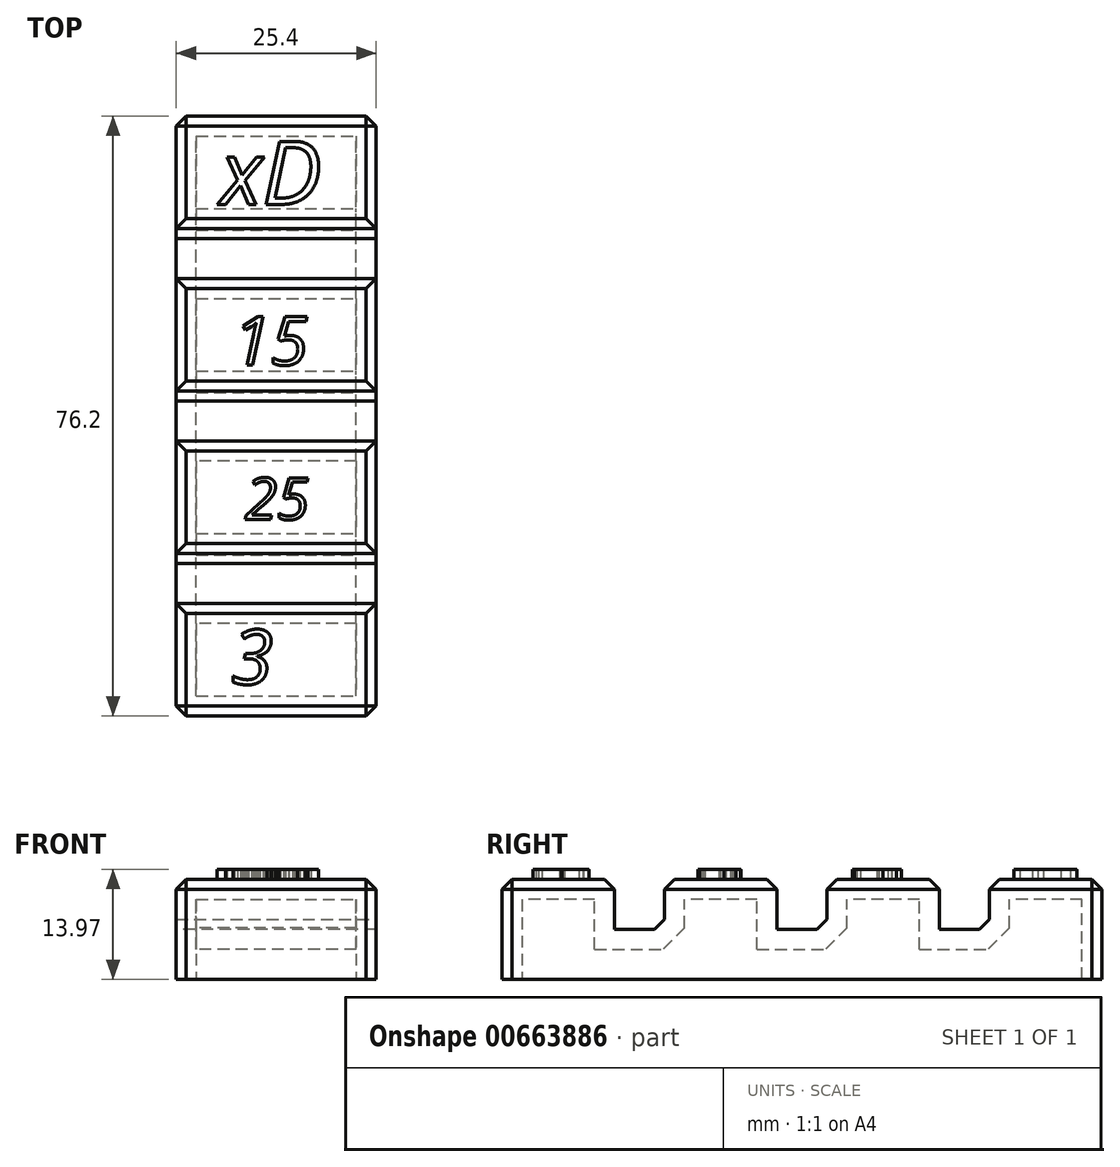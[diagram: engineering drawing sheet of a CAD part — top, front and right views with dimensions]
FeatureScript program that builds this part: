
annotation { "Feature Type Name" : "Feature", "Feature Type Description" : "" }
export const myFeature = defineFeature(function(context is Context, id is Id, definition is map)
    precondition{}
    {
        {
            var Q0;
            Q0=qCreatedBy(makeId("Top.planeOp"),FACE);
            var sketch = newSketch(context, id + "F0", { "sketchPlane" : qUnion([Q0])});
            skLineSegment(sketch, "E0.bottom", {"start": v(-12.7, -38.1) * mm, "end": v(12.7, -38.1) * mm});
            skLineSegment(sketch, "E0.top", {"start": v(-12.7, 38.1) * mm, "end": v(12.7, 38.1) * mm});
            skLineSegment(sketch, "E0.left", {"start": v(-12.7, -38.1) * mm, "end": v(-12.7, 38.1) * mm});
            skLineSegment(sketch, "E0.right", {"start": v(12.7, -38.1) * mm, "end": v(12.7, 38.1) * mm});
            skPoint(sketch, "E0.middle", {"position": v(0, 0) * mm});
            skSolve(sketch);
        }
        {
            var Q0;
            Q0 = qSketchRegion(id + "F0", true);
            extrude(context, id + "F1", {"entities" : qUnion([Q0]), "depth" : 12.7 * mm, "offsetDistance" : 25.4 * mm});
        }
        {
            var Q0;
            Q0=makeQuery(id+"F1.opExtrude","SWEPT_FACE",FACE,{"disambiguationData":[OSD([sQuery(id+"F0.wireOp",EDGE,"E0.left")])]});
            var sketch = newSketch(context, id + "F2", { "sketchPlane" : qUnion([Q0])});
            skLineSegment(sketch, "E1", {"start": v(-38.1, 6.35) * mm, "end": v(38.1, 6.35) * mm, "construction": true});
            skPoint(sketch, "E1.startSnap0", {"position": v(-38.1, 6.35) * mm});
            skLineSegment(sketch, "E2.bottom", {"start": v(3.18, 6.35) * mm, "end": v(-3.18, 6.35) * mm});
            skLineSegment(sketch, "E2.top", {"start": v(3.18, 19.05) * mm, "end": v(-3.18, 19.05) * mm});
            skLineSegment(sketch, "E2.left", {"start": v(3.18, 6.35) * mm, "end": v(3.18, 19.05) * mm});
            skLineSegment(sketch, "E2.right", {"start": v(-3.18, 6.35) * mm, "end": v(-3.18, 19.05) * mm});
            skPoint(sketch, "E2.middle", {"position": v(0, 12.7) * mm});
            skLineSegment(sketch, "E3.bottom", {"start": v(23.81, 6.35) * mm, "end": v(17.46, 6.35) * mm});
            skLineSegment(sketch, "E3.top", {"start": v(23.81, 19.05) * mm, "end": v(17.46, 19.05) * mm});
            skLineSegment(sketch, "E3.left", {"start": v(23.81, 6.35) * mm, "end": v(23.81, 19.05) * mm});
            skLineSegment(sketch, "E3.right", {"start": v(17.46, 6.35) * mm, "end": v(17.46, 19.05) * mm});
            skPoint(sketch, "E3.middle", {"position": v(20.64, 12.7) * mm});
            skLineSegment(sketch, "E4.bottom", {"start": v(-17.46, 6.35) * mm, "end": v(-23.81, 6.35) * mm});
            skLineSegment(sketch, "E4.top", {"start": v(-17.46, 19.05) * mm, "end": v(-23.81, 19.05) * mm});
            skLineSegment(sketch, "E4.left", {"start": v(-17.46, 6.35) * mm, "end": v(-17.46, 19.05) * mm});
            skLineSegment(sketch, "E4.right", {"start": v(-23.81, 6.35) * mm, "end": v(-23.81, 19.05) * mm});
            skPoint(sketch, "E4.middle", {"position": v(-20.64, 12.7) * mm});
            skSolve(sketch);
        }
        {
            var Q0;
            Q0 = qSketchRegion(id + "F2", true);
            extrude(context, id + "F3", {"entities" : qUnion([Q0]), "operationType" : NewBodyOperationType.REMOVE, "endBound" : BoundingType.THROUGH_ALL, "oppositeDirection" : true, "depth" : 25.4 * mm, "offsetDistance" : 25.4 * mm});
        }
        {
            var Q0;
            {var subQ0=sQuery(id+"F0.wireOp",EDGE,"E0.top");var subQ1=sQuery(id+"F0.wireOp",EDGE,"E0.left");var subQ2=sQuery(id+"F0.wireOp",EDGE,"E0.right");Q0=makeQuery(id+"F3.boolean.opBoolean","SPLIT",FACE,{"disambiguationData":[TD([makeQuery(id+"F1.opExtrude","SWEPT_FACE",FACE,{"disambiguationData":[OSD([subQ0])]})])],"derivedFrom":makeQuery(id+"F1.opExtrude","CAP_FACE",FACE,{"disambiguationData":[OSD([sQuery(id+"F0.wireOp",EDGE,"E0.bottom"),subQ0,subQ1,subQ2])],"isStart":false})});}
            var Q1;
            {var subQ0=sQuery(id+"F0.wireOp",EDGE,"E0.left");var subQ1=sQuery(id+"F0.wireOp",EDGE,"E0.right");Q1=makeQuery(id+"F3.boolean.opBoolean","SPLIT",FACE,{"disambiguationData":[TD([makeQuery(id+"F3.opExtrude","SWEPT_FACE",FACE,{"disambiguationData":[OSD([sQuery(id+"F2.wireOp",EDGE,"E2.right")])]})])],"derivedFrom":makeQuery(id+"F1.opExtrude","CAP_FACE",FACE,{"disambiguationData":[OSD([sQuery(id+"F0.wireOp",EDGE,"E0.bottom"),sQuery(id+"F0.wireOp",EDGE,"E0.top"),subQ0,subQ1])],"isStart":false})});}
            var Q2;
            {var subQ0=sQuery(id+"F0.wireOp",EDGE,"E0.left");var subQ1=sQuery(id+"F0.wireOp",EDGE,"E0.right");Q2=makeQuery(id+"F3.boolean.opBoolean","SPLIT",FACE,{"disambiguationData":[TD([makeQuery(id+"F3.opExtrude","SWEPT_FACE",FACE,{"disambiguationData":[OSD([sQuery(id+"F2.wireOp",EDGE,"E2.left")])]})])],"derivedFrom":makeQuery(id+"F1.opExtrude","CAP_FACE",FACE,{"disambiguationData":[OSD([sQuery(id+"F0.wireOp",EDGE,"E0.bottom"),sQuery(id+"F0.wireOp",EDGE,"E0.top"),subQ0,subQ1])],"isStart":false})});}
            var Q3;
            Q3=makeQuery(id+"F1.opExtrude","CAP_EDGE",EDGE,{"disambiguationData":[OSD([sQuery(id+"F0.wireOp",EDGE,"E0.bottom")])],"isStart":false});
            var Q4;
            {var subQ0=sQuery(id+"F0.wireOp",EDGE,"E0.bottom");var subQ1=sQuery(id+"F0.wireOp",EDGE,"E0.right");var subQ2=sQuery(id+"F0.wireOp",EDGE,"E0.left");Q4=makeQuery(id+"F3.boolean.opBoolean","SPLIT",FACE,{"disambiguationData":[TD([makeQuery(id+"F1.opExtrude","SWEPT_FACE",FACE,{"disambiguationData":[OSD([subQ0])]})])],"derivedFrom":makeQuery(id+"F1.opExtrude","CAP_FACE",FACE,{"disambiguationData":[OSD([subQ0,sQuery(id+"F0.wireOp",EDGE,"E0.top"),subQ2,subQ1])],"isStart":false})});}
            var Q5;
            Q5=makeQuery(id+"F3.boolean.opBoolean","COPY",EDGE,{"derivedFrom":makeQuery(id+"F3.opExtrude","SWEPT_EDGE",EDGE,{"disambiguationData":[OSD([sQuery(id+"F2.wireOp",EDGE,"E4.bottom"),sQuery(id+"F2.wireOp",EDGE,"E4.right")])]})});
            var Q6;
            Q6=makeQuery(id+"F3.boolean.opBoolean","COPY",EDGE,{"derivedFrom":makeQuery(id+"F3.opExtrude","CAP_EDGE",EDGE,{"disambiguationData":[OSD([sQuery(id+"F2.wireOp",EDGE,"E2.bottom")])],"isStart":true})});
            var Q7;
            Q7=makeQuery(id+"F3.boolean.opBoolean","COPY",EDGE,{"derivedFrom":makeQuery(id+"F3.opExtrude","CAP_EDGE",EDGE,{"disambiguationData":[OSD([sQuery(id+"F2.wireOp",EDGE,"E3.bottom")])],"isStart":true})});
            var Q8;
            Q8=makeQuery(id+"F3.boolean.opBoolean","COPY",EDGE,{"derivedFrom":makeQuery(id+"F3.opExtrude","CAP_EDGE",EDGE,{"disambiguationData":[OSD([sQuery(id+"F2.wireOp",EDGE,"E4.bottom")])],"isStart":true})});
            var Q9;
            Q9=makeQuery(id+"F3.boolean.opBoolean","COPY",EDGE,{"derivedFrom":makeQuery(id+"F3.opExtrude","SWEPT_EDGE",EDGE,{"disambiguationData":[OSD([sQuery(id+"F2.wireOp",EDGE,"E2.bottom"),sQuery(id+"F2.wireOp",EDGE,"E2.right")])]})});
            var Q10;
            Q10=makeQuery(id+"F3.boolean.opBoolean","COPY",EDGE,{"derivedFrom":makeQuery(id+"F3.opExtrude","SWEPT_EDGE",EDGE,{"disambiguationData":[OSD([sQuery(id+"F2.wireOp",EDGE,"E3.bottom"),sQuery(id+"F2.wireOp",EDGE,"E3.right")])]})});
            var Q11;
            Q11=makeQuery(id+"F1.opExtrude","SWEPT_EDGE",EDGE,{"disambiguationData":[OSD([sQuery(id+"F0.wireOp",EDGE,"E0.top"),sQuery(id+"F0.wireOp",EDGE,"E0.left")])]});
            var Q12;
            Q12=makeQuery(id+"F1.opExtrude","SWEPT_EDGE",EDGE,{"disambiguationData":[OSD([sQuery(id+"F0.wireOp",EDGE,"E0.bottom"),sQuery(id+"F0.wireOp",EDGE,"E0.left")])]});
            var Q13;
            Q13=makeQuery(id+"F1.opExtrude","SWEPT_EDGE",EDGE,{"disambiguationData":[OSD([sQuery(id+"F0.wireOp",EDGE,"E0.bottom"),sQuery(id+"F0.wireOp",EDGE,"E0.right")])]});
            var Q14;
            Q14=makeQuery(id+"F1.opExtrude","SWEPT_EDGE",EDGE,{"disambiguationData":[OSD([sQuery(id+"F0.wireOp",EDGE,"E0.top"),sQuery(id+"F0.wireOp",EDGE,"E0.right")])]});
            chamfer(context, id + "F4", {"entities" : qUnion([Q0, Q1, Q2, Q3, Q4, Q5, Q6, Q7, Q8, Q9, Q10, Q11, Q12, Q13, Q14]), "width" : 1.27 * mm, "tangentPropagation" : true});
        }
        {
            var Q0;
            Q0=makeQuery(id+"F1.opExtrude","CAP_FACE",FACE,{"disambiguationData":[OSD([sQuery(id+"F0.wireOp",EDGE,"E0.bottom"),sQuery(id+"F0.wireOp",EDGE,"E0.top"),sQuery(id+"F0.wireOp",EDGE,"E0.left"),sQuery(id+"F0.wireOp",EDGE,"E0.right")])],"isStart":true});
            shell(context, id + "F5", {"entities" : qUnion([Q0]), "thickness" : 2.54 * mm});
        }
        {
            var Q0;
            {var subQ0=sQuery(id+"F0.wireOp",EDGE,"E0.top");var subQ1=sQuery(id+"F0.wireOp",EDGE,"E0.left");var subQ2=sQuery(id+"F0.wireOp",EDGE,"E0.right");Q0=makeQuery(id+"F3.boolean.opBoolean","SPLIT",FACE,{"disambiguationData":[TD([makeQuery(id+"F1.opExtrude","SWEPT_FACE",FACE,{"disambiguationData":[OSD([subQ0])]})])],"derivedFrom":makeQuery(id+"F1.opExtrude","CAP_FACE",FACE,{"disambiguationData":[OSD([sQuery(id+"F0.wireOp",EDGE,"E0.bottom"),subQ0,subQ1,subQ2])],"isStart":false})});}
            var sketch = newSketch(context, id + "F6", { "sketchPlane" : qUnion([Q0])});
            skText(sketch, "E5", { "text": "3", "fontName": "OpenSans-Italic.ttf"});
            skLineSegment(sketch, "E6", {"start": v(0, -30.59) * mm, "end": v(11.37, -30.59) * mm, "construction": true});
            skLineSegment(sketch, "E7", {"start": v(0, -30.59) * mm, "end": v(-11.38, -30.59) * mm, "construction": true});
            const initialGuessF6  = {"E5": [-0.0057, -0.03407, 1, 0, 0.00696]};
            skSetInitialGuess(sketch, initialGuessF6);
            skSolve(sketch);
        }
        {
            var Q0;
            Q0 = qSketchRegion(id + "F6", true);
            extrude(context, id + "F7", {"entities" : qUnion([Q0]), "operationType" : NewBodyOperationType.ADD, "depth" : 1.27 * mm, "offsetDistance" : 25.4 * mm});
        }
        {
            var Q0;
            {var subQ0=sQuery(id+"F0.wireOp",EDGE,"E0.left");var subQ1=sQuery(id+"F0.wireOp",EDGE,"E0.right");Q0=makeQuery(id+"F3.boolean.opBoolean","SPLIT",FACE,{"disambiguationData":[TD([makeQuery(id+"F3.opExtrude","SWEPT_FACE",FACE,{"disambiguationData":[OSD([sQuery(id+"F2.wireOp",EDGE,"E2.left")])]})])],"derivedFrom":makeQuery(id+"F1.opExtrude","CAP_FACE",FACE,{"disambiguationData":[OSD([sQuery(id+"F0.wireOp",EDGE,"E0.bottom"),sQuery(id+"F0.wireOp",EDGE,"E0.top"),subQ0,subQ1])],"isStart":false})});}
            var sketch = newSketch(context, id + "F8", { "sketchPlane" : qUnion([Q0])});
            skText(sketch, "E8", { "text": "25", "fontName": "OpenSans-Italic.ttf"});
            const initialGuessF8  = {"E8": [-0.004, -0.01316, 1, 0, 0.00535]};
            skSetInitialGuess(sketch, initialGuessF8);
            skSolve(sketch);
        }
        {
            var Q0;
            Q0 = qSketchRegion(id + "F8", true);
            extrude(context, id + "F9", {"entities" : qUnion([Q0]), "operationType" : NewBodyOperationType.ADD, "depth" : 1.27 * mm, "offsetDistance" : 25.4 * mm});
        }
        {
            var Q0;
            {var subQ0=sQuery(id+"F0.wireOp",EDGE,"E0.left");var subQ1=sQuery(id+"F0.wireOp",EDGE,"E0.right");Q0=makeQuery(id+"F3.boolean.opBoolean","SPLIT",FACE,{"disambiguationData":[TD([makeQuery(id+"F3.opExtrude","SWEPT_FACE",FACE,{"disambiguationData":[OSD([sQuery(id+"F2.wireOp",EDGE,"E2.right")])]})])],"derivedFrom":makeQuery(id+"F1.opExtrude","CAP_FACE",FACE,{"disambiguationData":[OSD([sQuery(id+"F0.wireOp",EDGE,"E0.bottom"),sQuery(id+"F0.wireOp",EDGE,"E0.top"),subQ0,subQ1])],"isStart":false})});}
            var sketch = newSketch(context, id + "F10", { "sketchPlane" : qUnion([Q0])});
            skText(sketch, "E9", { "text": "15", "fontName": "OpenSans-Italic.ttf"});
            const initialGuessF10  = {"E9": [-0.00548, 0.00647, 1, 0, 0.00623]};
            skSetInitialGuess(sketch, initialGuessF10);
            skSolve(sketch);
        }
        {
            var Q0;
            Q0 = qSketchRegion(id + "F10", true);
            extrude(context, id + "F11", {"entities" : qUnion([Q0]), "operationType" : NewBodyOperationType.ADD, "depth" : 1.27 * mm, "offsetDistance" : 25.4 * mm});
        }
        {
            var Q0;
            {var subQ0=sQuery(id+"F0.wireOp",EDGE,"E0.top");var subQ1=sQuery(id+"F0.wireOp",EDGE,"E0.left");var subQ2=sQuery(id+"F0.wireOp",EDGE,"E0.right");Q0=makeQuery(id+"F3.boolean.opBoolean","SPLIT",FACE,{"disambiguationData":[TD([makeQuery(id+"F1.opExtrude","SWEPT_FACE",FACE,{"disambiguationData":[OSD([subQ0])]})])],"derivedFrom":makeQuery(id+"F1.opExtrude","CAP_FACE",FACE,{"disambiguationData":[OSD([sQuery(id+"F0.wireOp",EDGE,"E0.bottom"),subQ0,subQ1,subQ2])],"isStart":false})});}
            var sketch = newSketch(context, id + "F12", { "sketchPlane" : qUnion([Q0])});
            skText(sketch, "E10", { "text": "xD", "fontName": "OpenSans-Italic.ttf"});
            const initialGuessF12  = {"E10": [-0.0071, 0.02688, 1, 0, 0.00808]};
            skSetInitialGuess(sketch, initialGuessF12);
            skSolve(sketch);
        }
        {
            var Q0;
            Q0 = qSketchRegion(id + "F12", true);
            extrude(context, id + "F13", {"entities" : qUnion([Q0]), "operationType" : NewBodyOperationType.ADD, "depth" : 1.27 * mm, "offsetDistance" : 25.4 * mm});
        }
    });
